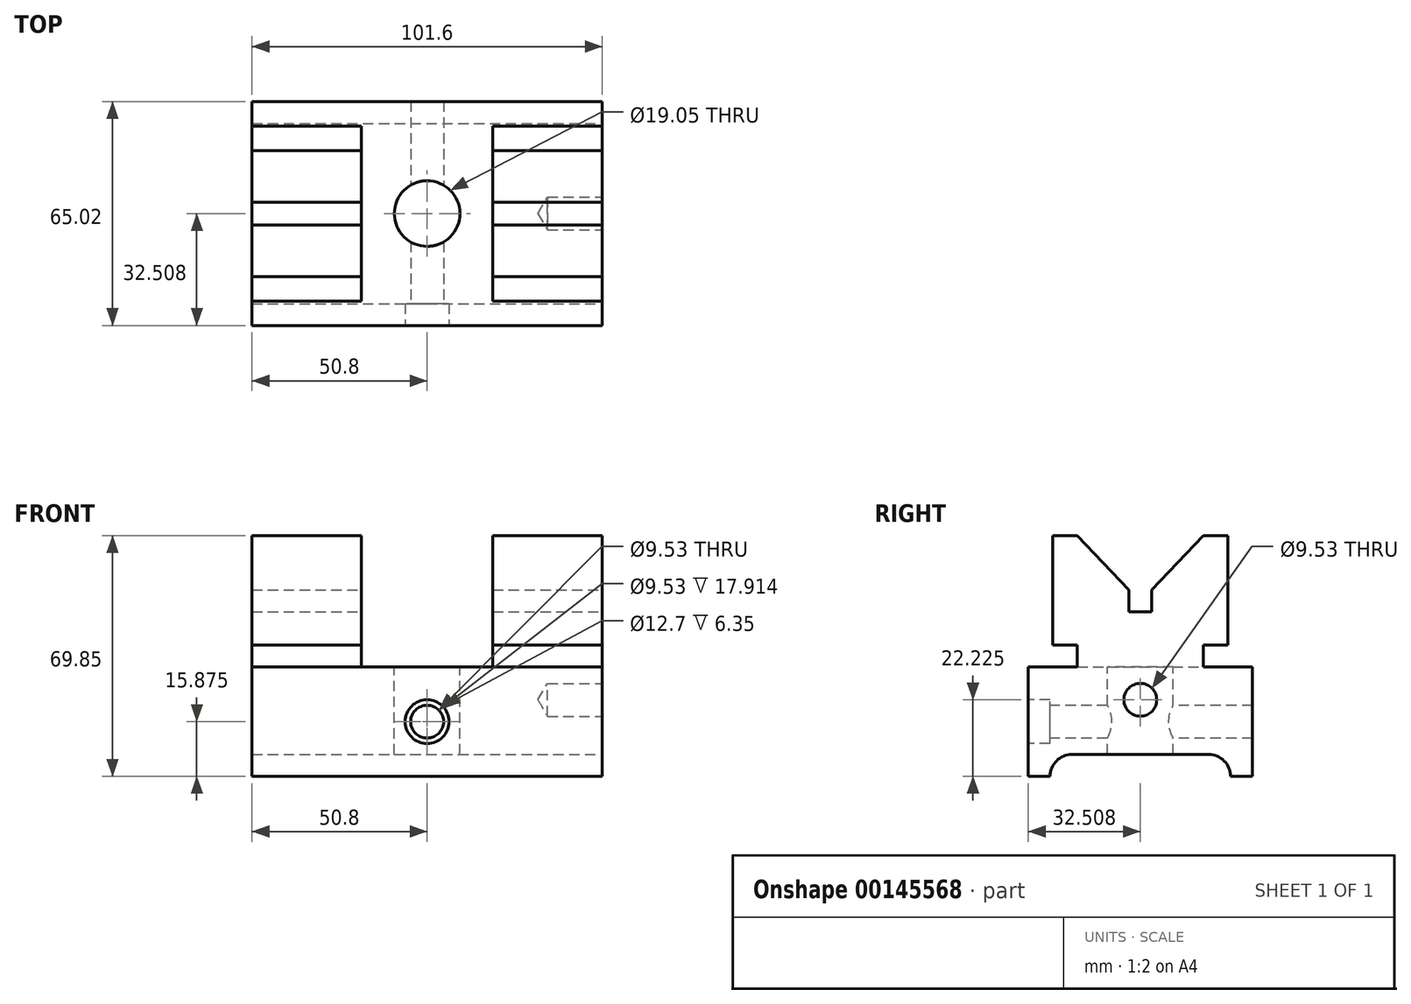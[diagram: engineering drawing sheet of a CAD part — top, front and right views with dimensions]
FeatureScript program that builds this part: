
annotation { "Feature Type Name" : "Feature", "Feature Type Description" : "" }
export const myFeature = defineFeature(function(context is Context, id is Id, definition is map)
    precondition{}
    {
        {
            var Q0;
            Q0=qCreatedBy(makeId("Front.planeOp"),FACE);
            var sketch = newSketch(context, id + "F0", { "sketchPlane" : qUnion([Q0])});
            skLineSegment(sketch, "E0", {"start": v(-50.8, 0) * mm, "end": v(-50.8, 69.85) * mm});
            skLineSegment(sketch, "E1", {"start": v(-50.8, 69.85) * mm, "end": v(-19.05, 69.85) * mm});
            skLineSegment(sketch, "E2", {"start": v(-19.05, 69.85) * mm, "end": v(-19.05, 31.75) * mm});
            skLineSegment(sketch, "E3", {"start": v(-19.05, 31.75) * mm, "end": v(19.05, 31.75) * mm});
            skLineSegment(sketch, "E4", {"start": v(19.05, 31.75) * mm, "end": v(19.05, 69.85) * mm});
            skLineSegment(sketch, "E5", {"start": v(19.05, 69.85) * mm, "end": v(50.8, 69.85) * mm});
            skLineSegment(sketch, "E6", {"start": v(50.8, 69.85) * mm, "end": v(50.8, 0) * mm});
            skLineSegment(sketch, "E7", {"start": v(-50.8, 0) * mm, "end": v(50.8, 0) * mm});
            skPoint(sketch, "E8", {"position": v(0, 15.88) * mm});
            skSolve(sketch);
        }
        {
            var Q0;
            Q0 = qSketchRegion(id + "F0", true);
            extrude(context, id + "F1", {"entities" : qUnion([Q0]), "depth" : 65.02 * mm});
        }
        {
            var Q0;
            Q0=makeQuery(id+"F1.opExtrude","CAP_FACE",FACE,{"disambiguationData":[OSD([sQuery(id+"F0.wireOp",EDGE,"E0"),sQuery(id+"F0.wireOp",EDGE,"E1"),sQuery(id+"F0.wireOp",EDGE,"E2"),sQuery(id+"F0.wireOp",EDGE,"E3"),sQuery(id+"F0.wireOp",EDGE,"E4"),sQuery(id+"F0.wireOp",EDGE,"E5"),sQuery(id+"F0.wireOp",EDGE,"E6"),sQuery(id+"F0.wireOp",EDGE,"E7")])],"isStart":false});
            var sketch = newSketch(context, id + "F2", { "sketchPlane" : qUnion([Q0])});
            skPoint(sketch, "E9.0", {"position": v(0, 15.88) * mm});
            skSolve(sketch);
        }
        {
            var Q0;
            Q0=sQuery(id+"F2.wireOp",VERTEX,"E9.0");
            var Q1;
            Q1=makeQuery(id+"F1.opExtrude","SWEPT_BODY",BODY,{"disambiguationData":[OSD([sQuery(id+"F0.wireOp",EDGE,"E0"),sQuery(id+"F0.wireOp",EDGE,"E1"),sQuery(id+"F0.wireOp",EDGE,"E2"),sQuery(id+"F0.wireOp",EDGE,"E3"),sQuery(id+"F0.wireOp",EDGE,"E4"),sQuery(id+"F0.wireOp",EDGE,"E5"),sQuery(id+"F0.wireOp",EDGE,"E6"),sQuery(id+"F0.wireOp",EDGE,"E7")])]});
            hole(context, id + "F3", {"style" : HoleStyle.C_BORE, "endStyle" : HoleEndStyle.THROUGH, "holeDiameter" : 9.52 * mm, "cBoreDiameter" : 12.7 * mm, "cBoreDepth" : 6.35 * mm, "locations" : qUnion([Q0]), "scope" : qUnion([Q1]), "isTappedThrough" : true});
        }
        {
            var Q0;
            Q0=makeQuery(id+"F1.opExtrude","SWEPT_FACE",FACE,{"disambiguationData":[OSD([sQuery(id+"F0.wireOp",EDGE,"E1")])]});
            var sketch = newSketch(context, id + "F4", { "sketchPlane" : qUnion([Q0])});
            skLineSegment(sketch, "E10", {"start": v(-50.8, -65.02) * mm, "end": v(-50.8, -57.91) * mm});
            skLineSegment(sketch, "E11", {"start": v(-50.8, -57.91) * mm, "end": v(-19.05, -57.91) * mm});
            skLineSegment(sketch, "E12", {"start": v(-19.05, -57.91) * mm, "end": v(-19.05, -65.02) * mm});
            skLineSegment(sketch, "E13", {"start": v(-19.05, -65.02) * mm, "end": v(-50.8, -65.02) * mm});
            skSolve(sketch);
        }
        {
            var Q0;
            Q0 = qSketchRegion(id + "F4", true);
            extrude(context, id + "F5", {"entities" : qUnion([Q0]), "operationType" : NewBodyOperationType.REMOVE, "oppositeDirection" : true, "depth" : 38.1 * mm});
        }
        {
            var Q0;
            Q0=makeQuery(id+"F1.opExtrude","SWEPT_FACE",FACE,{"disambiguationData":[OSD([sQuery(id+"F0.wireOp",EDGE,"E6")])]});
            var sketch = newSketch(context, id + "F6", { "sketchPlane" : qUnion([Q0])});
            skLineSegment(sketch, "E14.bottom", {"start": v(-65.02, 69.85) * mm, "end": v(-57.91, 69.85) * mm});
            skLineSegment(sketch, "E14.top", {"start": v(-65.02, 31.75) * mm, "end": v(-57.91, 31.75) * mm});
            skLineSegment(sketch, "E14.left", {"start": v(-65.02, 69.85) * mm, "end": v(-65.02, 31.75) * mm});
            skLineSegment(sketch, "E14.right", {"start": v(-57.91, 69.85) * mm, "end": v(-57.91, 31.75) * mm});
            skLineSegment(sketch, "E15.bottom", {"start": v(0, 69.85) * mm, "end": v(-7.11, 69.85) * mm});
            skLineSegment(sketch, "E15.top", {"start": v(0, 31.75) * mm, "end": v(-7.11, 31.75) * mm});
            skLineSegment(sketch, "E15.left", {"start": v(0, 69.85) * mm, "end": v(0, 31.75) * mm});
            skLineSegment(sketch, "E15.right", {"start": v(-7.11, 69.85) * mm, "end": v(-7.11, 31.75) * mm});
            skSolve(sketch);
        }
        {
            var Q0;
            Q0 = qSketchRegion(id + "F6", true);
            extrude(context, id + "F7", {"entities" : qUnion([Q0]), "operationType" : NewBodyOperationType.REMOVE, "endBound" : BoundingType.THROUGH_ALL, "oppositeDirection" : true, "depth" : 25.4 * mm});
        }
        {
            var Q0;
            Q0=makeQuery(id+"F1.opExtrude","SWEPT_FACE",FACE,{"disambiguationData":[OSD([sQuery(id+"F0.wireOp",EDGE,"E6")])]});
            var sketch = newSketch(context, id + "F8", { "sketchPlane" : qUnion([Q0])});
            skArc(sketch, "E16", {"start": v(-52.32, 6.35) * mm, "mid": v(-56.81, 4.5) * mm, "end": v(-58.67, 0) * mm});
            skLineSegment(sketch, "E17", {"start": v(-52.32, 6.35) * mm, "end": v(-12.7, 6.35) * mm});
            skArc(sketch, "E18", {"start": v(-6.35, 0) * mm, "mid": v(-8.2, 4.5) * mm, "end": v(-12.7, 6.35) * mm});
            skLineSegment(sketch, "E19", {"start": v(-58.67, 0) * mm, "end": v(-6.35, 0) * mm});
            skSolve(sketch);
        }
        {
            var Q0;
            Q0 = qSketchRegion(id + "F8", true);
            extrude(context, id + "F9", {"entities" : qUnion([Q0]), "operationType" : NewBodyOperationType.REMOVE, "endBound" : BoundingType.THROUGH_ALL, "oppositeDirection" : true, "depth" : 25.4 * mm});
        }
        {
            var Q0;
            Q0=makeQuery(id+"F1.opExtrude","SWEPT_FACE",FACE,{"disambiguationData":[OSD([sQuery(id+"F0.wireOp",EDGE,"E6")])]});
            var sketch = newSketch(context, id + "F10", { "sketchPlane" : qUnion([Q0])});
            skPoint(sketch, "E20", {"position": v(-32.51, 22.22) * mm});
            skSolve(sketch);
        }
        {
            var Q0;
            Q0=sQuery(id+"F10.wireOp",VERTEX,"E20");
            var Q1;
            Q1=makeQuery(id+"F1.opExtrude","SWEPT_BODY",BODY,{"disambiguationData":[OSD([sQuery(id+"F0.wireOp",EDGE,"E0"),sQuery(id+"F0.wireOp",EDGE,"E1"),sQuery(id+"F0.wireOp",EDGE,"E2"),sQuery(id+"F0.wireOp",EDGE,"E3"),sQuery(id+"F0.wireOp",EDGE,"E4"),sQuery(id+"F0.wireOp",EDGE,"E5"),sQuery(id+"F0.wireOp",EDGE,"E6"),sQuery(id+"F0.wireOp",EDGE,"E7")])]});
            hole(context, id + "F11", {"style" : HoleStyle.SIMPLE, "endStyle" : HoleEndStyle.BLIND, "holeDiameter" : 9.52 * mm, "holeDepth" : 15.88 * mm, "locations" : qUnion([Q0]), "scope" : qUnion([Q1])});
        }
        {
            var Q0;
            Q0=makeQuery(id+"F1.opExtrude","SWEPT_FACE",FACE,{"disambiguationData":[OSD([sQuery(id+"F0.wireOp",EDGE,"E6")])]});
            var sketch = newSketch(context, id + "F12", { "sketchPlane" : qUnion([Q0])});
            skLineSegment(sketch, "E21.bottom", {"start": v(-35.81, 54.1) * mm, "end": v(-29.2, 54.1) * mm});
            skLineSegment(sketch, "E21.top", {"start": v(-35.81, 47.75) * mm, "end": v(-29.2, 47.75) * mm});
            skLineSegment(sketch, "E21.left", {"start": v(-35.81, 54.1) * mm, "end": v(-35.81, 47.75) * mm});
            skLineSegment(sketch, "E21.right", {"start": v(-29.2, 54.1) * mm, "end": v(-29.2, 47.75) * mm});
            skSolve(sketch);
        }
        {
            var Q0;
            Q0 = qSketchRegion(id + "F12", true);
            extrude(context, id + "F13", {"entities" : qUnion([Q0]), "operationType" : NewBodyOperationType.REMOVE, "endBound" : BoundingType.THROUGH_ALL, "oppositeDirection" : true, "depth" : 25.4 * mm});
        }
        {
            var Q0;
            Q0=makeQuery(id+"F1.opExtrude","SWEPT_FACE",FACE,{"disambiguationData":[OSD([sQuery(id+"F0.wireOp",EDGE,"E6")])]});
            var sketch = newSketch(context, id + "F14", { "sketchPlane" : qUnion([Q0])});
            skLineSegment(sketch, "E22", {"start": v(-35.81, 54.1) * mm, "end": v(-50.8, 69.85) * mm});
            skLineSegment(sketch, "E23", {"start": v(-50.8, 69.85) * mm, "end": v(-14.22, 69.85) * mm});
            skLineSegment(sketch, "E24", {"start": v(-14.22, 69.85) * mm, "end": v(-29.2, 54.1) * mm});
            skLineSegment(sketch, "E25", {"start": v(-29.2, 54.1) * mm, "end": v(-35.81, 54.1) * mm});
            skSolve(sketch);
        }
        {
            var Q0;
            Q0 = qSketchRegion(id + "F14", true);
            extrude(context, id + "F15", {"entities" : qUnion([Q0]), "operationType" : NewBodyOperationType.REMOVE, "endBound" : BoundingType.THROUGH_ALL, "oppositeDirection" : true, "depth" : 25.4 * mm});
        }
        {
            var Q0;
            Q0=makeQuery(id+"F1.opExtrude","SWEPT_FACE",FACE,{"disambiguationData":[OSD([sQuery(id+"F0.wireOp",EDGE,"E6")])]});
            var sketch = newSketch(context, id + "F16", { "sketchPlane" : qUnion([Q0])});
            skLineSegment(sketch, "E26.bottom", {"start": v(-7.11, 31.75) * mm, "end": v(-14.22, 31.75) * mm});
            skLineSegment(sketch, "E26.top", {"start": v(-7.11, 38.1) * mm, "end": v(-14.22, 38.1) * mm});
            skLineSegment(sketch, "E26.left", {"start": v(-7.11, 31.75) * mm, "end": v(-7.11, 38.1) * mm});
            skLineSegment(sketch, "E26.right", {"start": v(-14.22, 31.75) * mm, "end": v(-14.22, 38.1) * mm});
            skLineSegment(sketch, "E27.bottom", {"start": v(-57.91, 31.75) * mm, "end": v(-50.8, 31.75) * mm});
            skLineSegment(sketch, "E27.top", {"start": v(-57.91, 38.1) * mm, "end": v(-50.8, 38.1) * mm});
            skLineSegment(sketch, "E27.left", {"start": v(-57.91, 31.75) * mm, "end": v(-57.91, 38.1) * mm});
            skLineSegment(sketch, "E27.right", {"start": v(-50.8, 31.75) * mm, "end": v(-50.8, 38.1) * mm});
            skSolve(sketch);
        }
        {
            var Q0;
            Q0 = qSketchRegion(id + "F16", true);
            extrude(context, id + "F17", {"entities" : qUnion([Q0]), "operationType" : NewBodyOperationType.REMOVE, "endBound" : BoundingType.THROUGH_ALL, "oppositeDirection" : true, "depth" : 25.4 * mm});
        }
        {
            var Q0;
            Q0=makeQuery(id+"F17.boolean.opBoolean","MERGE",FACE,{"derivedFrom":[makeQuery(id+"F7.boolean.opBoolean","MERGE",FACE,{"derivedFrom":[makeQuery(id+"F5.boolean.opBoolean","MERGE",FACE,{"derivedFrom":[makeQuery(id+"F1.opExtrude","SWEPT_FACE",FACE,{"disambiguationData":[OSD([sQuery(id+"F0.wireOp",EDGE,"E3")])]}),makeQuery(id+"F5.opExtrude","CAP_FACE",FACE,{"disambiguationData":[OSD([sQuery(id+"F4.wireOp",EDGE,"E10"),sQuery(id+"F4.wireOp",EDGE,"E11"),sQuery(id+"F4.wireOp",EDGE,"E12"),sQuery(id+"F4.wireOp",EDGE,"E13")])],"isStart":false})]}),makeQuery(id+"F7.opExtrude","SWEPT_FACE",FACE,{"disambiguationData":[OSD([sQuery(id+"F6.wireOp",EDGE,"E14.top")])]}),makeQuery(id+"F7.opExtrude","SWEPT_FACE",FACE,{"disambiguationData":[OSD([sQuery(id+"F6.wireOp",EDGE,"E15.top")])]})]}),makeQuery(id+"F17.opExtrude","SWEPT_FACE",FACE,{"disambiguationData":[OSD([sQuery(id+"F16.wireOp",EDGE,"E26.bottom")])]}),makeQuery(id+"F17.opExtrude","SWEPT_FACE",FACE,{"disambiguationData":[OSD([sQuery(id+"F16.wireOp",EDGE,"E27.bottom")])]})]});
            var sketch = newSketch(context, id + "F18", { "sketchPlane" : qUnion([Q0])});
            skCircle(sketch, "E28", {"center": v(0, -32.51) * mm, "radius": 9.53 * mm});
            skSolve(sketch);
        }
        {
            var Q0;
            Q0 = qSketchRegion(id + "F18", true);
            extrude(context, id + "F19", {"entities" : qUnion([Q0]), "operationType" : NewBodyOperationType.REMOVE, "endBound" : BoundingType.THROUGH_ALL, "oppositeDirection" : true, "depth" : 25.4 * mm});
        }
    });
